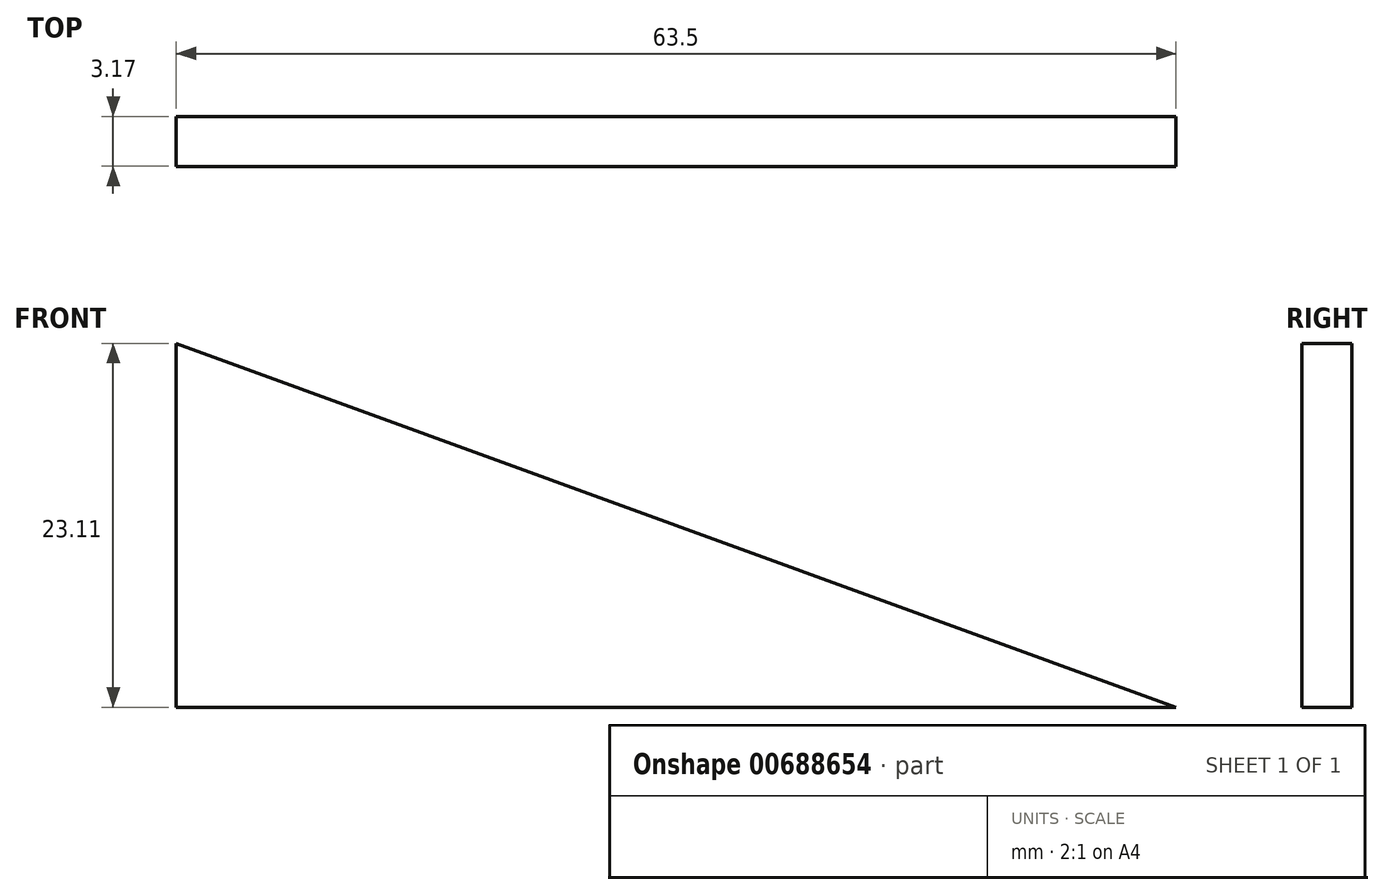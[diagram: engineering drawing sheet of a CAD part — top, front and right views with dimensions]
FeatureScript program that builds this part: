
annotation { "Feature Type Name" : "Feature", "Feature Type Description" : "" }
export const myFeature = defineFeature(function(context is Context, id is Id, definition is map)
    precondition{}
    {
        {
            var Q0;
            Q0=qCreatedBy(makeId("Front.planeOp"),FACE);
            var sketch = newSketch(context, id + "F0", { "sketchPlane" : qUnion([Q0])});
            skLineSegment(sketch, "E0", {"start": v(-32.03, -23.11) * mm, "end": v(31.47, -23.11) * mm});
            skLineSegment(sketch, "E1", {"start": v(31.47, -23.11) * mm, "end": v(-32.03, 0) * mm});
            skLineSegment(sketch, "E2", {"start": v(-32.03, -23.11) * mm, "end": v(-32.03, 0) * mm});
            skSolve(sketch);
        }
        {
            var Q0;
            Q0 = qSketchRegion(id + "F0", true);
            extrude(context, id + "F1", {"entities" : qUnion([Q0]), "depth" : 3.17 * mm, "offsetDistance" : 25.4 * mm});
        }
    });
